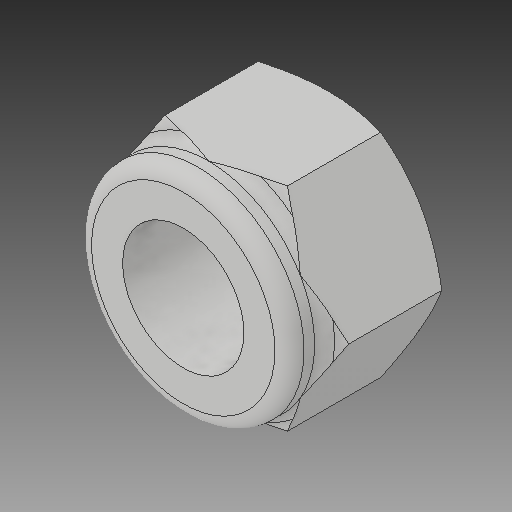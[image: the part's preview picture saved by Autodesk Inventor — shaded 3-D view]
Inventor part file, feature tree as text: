
AUTODESK INVENTOR PART (.ipt)
format: ipt  version: 2017 (Build 210142000, 142)  size: 176,640 bytes
history: native  units: in
note: dims shown in document units (in); Inventor stores cm internally (conversion verified against a paired STEP export)
features: fillet x1
ambient origin geometry x8: Origin, YZ Plane, XZ Plane, XY Plane, X Axis, Y Axis, Z Axis, Center Point
bodies: Solid1 (feature_tree)
feature tree (1):
  fillet  "Fillet7"  [1 undecoded]
note: 1 required parameter value undecoded (feature->parameter linkage not recoverable at this tier; creation-order binding heuristic only, values carry confidence <= 0.55)
